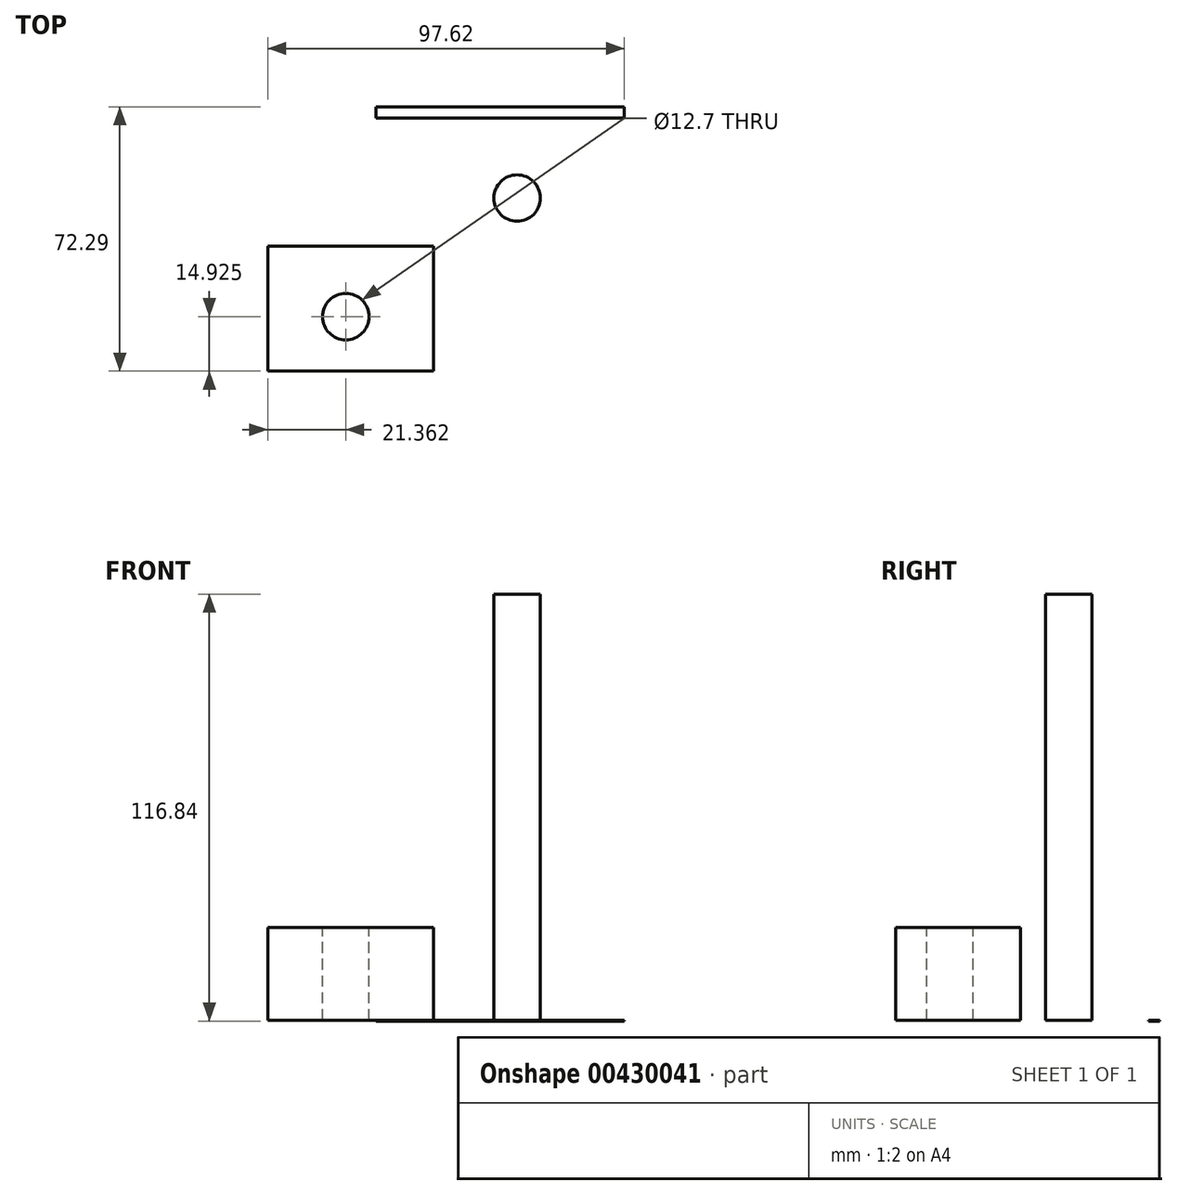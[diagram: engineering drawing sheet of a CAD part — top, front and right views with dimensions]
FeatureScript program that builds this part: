
annotation { "Feature Type Name" : "Feature", "Feature Type Description" : "" }
export const myFeature = defineFeature(function(context is Context, id is Id, definition is map)
    precondition{}
    {
        {
            var Q0;
            Q0=qCreatedBy(makeId("Top.planeOp"),FACE);
            var sketch = newSketch(context, id + "F0", { "sketchPlane" : qUnion([Q0])});
            skLineSegment(sketch, "E0.bottom", {"start": v(-29.7, 15.38) * mm, "end": v(38.3, 15.38) * mm});
            skLineSegment(sketch, "E0.top", {"start": v(-29.7, 12.36) * mm, "end": v(38.3, 12.36) * mm});
            skLineSegment(sketch, "E0.left", {"start": v(-29.7, 15.38) * mm, "end": v(-29.7, 12.36) * mm});
            skLineSegment(sketch, "E0.right", {"start": v(38.3, 15.38) * mm, "end": v(38.3, 12.36) * mm});
            skSolve(sketch);
        }
        {
            var Q0;
            Q0=makeQuery(id+"F0.imprint","IMPRINT",FACE,{"disambiguationData":[TD([[makeQuery(id+"F0.imprint","IMPRINT",EDGE,{"derivedFrom":sQuery(id+"F0.wireOp",EDGE,"E0.bottom")}),-1.0]])]});
            extrude(context, id + "F1", {"entities" : qUnion([Q0]), "oppositeDirection" : true, "depth" : 0.25 * mm});
        }
        {
            var Q0;
            Q0=qCreatedBy(makeId("Top.planeOp"),FACE);
            var sketch = newSketch(context, id + "F2", { "sketchPlane" : qUnion([Q0])});
            skLineSegment(sketch, "E1.bottom", {"start": v(-59.33, -22.68) * mm, "end": v(-13.98, -22.68) * mm});
            skLineSegment(sketch, "E1.top", {"start": v(-59.33, -56.9) * mm, "end": v(-13.98, -56.9) * mm});
            skLineSegment(sketch, "E1.left", {"start": v(-59.33, -22.68) * mm, "end": v(-59.33, -56.9) * mm});
            skLineSegment(sketch, "E1.right", {"start": v(-13.98, -22.68) * mm, "end": v(-13.98, -56.9) * mm});
            skSolve(sketch);
        }
        {
            var Q0;
            Q0=makeQuery(id+"F2.imprint","IMPRINT",FACE,{"disambiguationData":[TD([[makeQuery(id+"F2.imprint","IMPRINT",EDGE,{"derivedFrom":sQuery(id+"F2.wireOp",EDGE,"E1.bottom")}),-1.0]])]});
            extrude(context, id + "F3", {"entities" : qUnion([Q0]), "depth" : 25.4 * mm});
        }
        {
            var Q0;
            Q0=makeQuery(id+"F3.opExtrude","CAP_FACE",FACE,{"disambiguationData":[OSD([sQuery(id+"F2.wireOp",EDGE,"E1.bottom"),sQuery(id+"F2.wireOp",EDGE,"E1.top"),sQuery(id+"F2.wireOp",EDGE,"E1.left"),sQuery(id+"F2.wireOp",EDGE,"E1.right")])],"isStart":false});
            var sketch = newSketch(context, id + "F4", { "sketchPlane" : qUnion([Q0])});
            skCircle(sketch, "E2", {"center": v(-37.97, -41.98) * mm, "radius": 6.35 * mm});
            skSolve(sketch);
        }
        {
            var Q0;
            Q0=sQuery(id+"F4.wireOp",VERTEX,"E2.center");
            var Q1;
            Q1=makeQuery(id+"F3.opExtrude","SWEPT_BODY",BODY,{"disambiguationData":[OSD([sQuery(id+"F2.wireOp",EDGE,"E1.bottom"),sQuery(id+"F2.wireOp",EDGE,"E1.top"),sQuery(id+"F2.wireOp",EDGE,"E1.left"),sQuery(id+"F2.wireOp",EDGE,"E1.right")])]});
            hole(context, id + "F5", {"style" : HoleStyle.SIMPLE, "endStyle" : HoleEndStyle.THROUGH, "holeDiameter" : 12.7 * mm, "isTappedThrough" : true, "tappedDepth" : 12.7 * mm, "tapClearance" : 3, "locations" : qUnion([Q0]), "scope" : qUnion([Q1])});
        }
        {
            var Q0;
            Q0=qCreatedBy(makeId("Top.planeOp"),FACE);
            var sketch = newSketch(context, id + "F6", { "sketchPlane" : qUnion([Q0])});
            skCircle(sketch, "E3", {"center": v(8.93, -9.55) * mm, "radius": 6.35 * mm});
            skSolve(sketch);
        }
        {
            var Q0;
            Q0=makeQuery(id+"F6.imprint","IMPRINT",FACE,{"disambiguationData":[TD([[makeQuery(id+"F6.imprint","IMPRINT",EDGE,{"derivedFrom":sQuery(id+"F6.wireOp",EDGE,"E3")}),1.0]])]});
            extrude(context, id + "F7", {"entities" : qUnion([Q0]), "depth" : 116.6 * mm});
        }
    });
